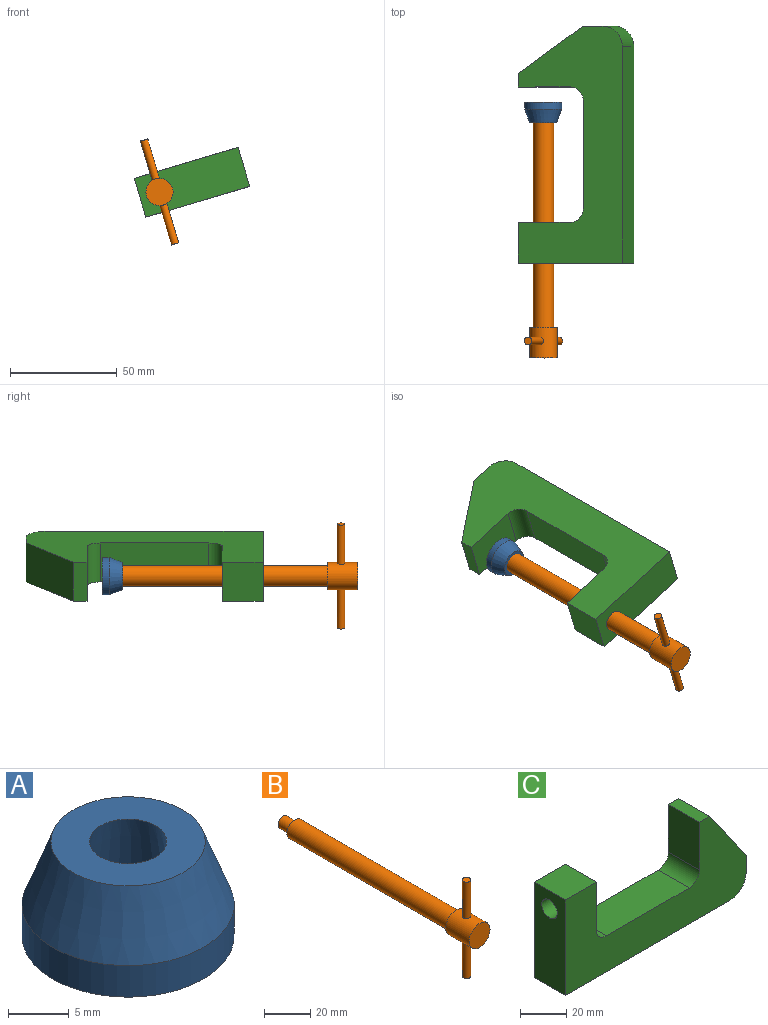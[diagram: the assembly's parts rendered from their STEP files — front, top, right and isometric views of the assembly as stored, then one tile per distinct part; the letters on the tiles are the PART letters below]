
ASSEMBLY  parts=3 mates=3
PART A: 5 faces, bbox 17.4x17.4x9.5 mm
  f0: cylinder r=8.72mm len=17.45mm, axis (0,0,-1), area 174.1mm2, adj f1,f3
  f1: plane 17.45x17.45mm, normal (0,0,-1), area 167.9mm2, adj f0,f4
  f2: plane 12.7x12.7mm, normal (0,0,1), area 95mm2, adj f3,f4
  f3: cone r=8.72mm half-angle=20.5deg, axis (0,0,-1), area 321.1mm2, adj f0,f2
  f4: cone r=4.76mm half-angle=9.5deg, axis (0,0,-1), area 240.8mm2, adj f1,f2
PART B: 11 faces, bbox 12.7x119.8x50.8 mm
  f0: cylinder r=4.76mm len=98.43mm, axis (0,-1,0), area 2945.2mm2, adj f1,f4
  f1: plane 9.53x9.53mm, normal (0,1,0), area 42.1mm2, adj f0,f9
  f2: cylinder r=6.35mm len=14.28mm, axis (0,1,0), area 549.1mm2, adj f3,f4,f6,f7
  f3: plane 12.7x12.7mm, normal (0,-1,0), area 126.7mm2, adj f2
  f4: plane 12.7x12.7mm, normal (0,1,0), area 55.4mm2, adj f0,f2
  f5: plane 3.59x3.59mm, normal (0,0,-1), area 10.1mm2, adj f6
  f6: cylinder r=1.8mm len=19.31mm, axis (0,0,1), area 216.3mm2, adj f2,f5
  f7: cylinder r=1.8mm len=19.31mm, axis (0,0,1), area 216.3mm2, adj f2,f8
  f8: plane 3.59x3.59mm, normal (0,0,1), area 10.1mm2, adj f7
  f9: cylinder r=3.05mm len=7.14mm, axis (0,-1,0), area 136.7mm2, adj f1,f10
  f10: plane 6.1x6.1mm, normal (0,1,0), area 29.2mm2, adj f9
PART C: 15 faces, bbox 111.1x19.1x50.8 mm
  f0: plane 19.05x9.7mm, normal (1,0,0), area 184.9mm2, adj f1,f11,f12,f13
  f1: plane 31.75x22.22mm, normal (0.82,0,0.57), area 738.3mm2, adj f0,f2,f12,f13
  f2: plane 19.05x6.35mm, normal (0,0,1), area 121mm2, adj f1,f3,f12,f13
  f3: plane 25.4x19.05mm, normal (-1,0,0), area 483.9mm2, adj f2,f4,f12,f13
  f4: cylinder r=6.35mm len=19.05mm, axis (0,1,0), area 190mm2, adj f3,f5,f12,f13
  f5: plane 50.8x19.05mm, normal (0,0,1), area 967.7mm2, adj f4,f6,f12,f13
  f6: cylinder r=6.35mm len=19.05mm, axis (0,1,0), area 190mm2, adj f5,f7,f12,f13
  f7: plane 25.4x19.05mm, normal (1,0,0), area 412.6mm2, adj f6,f8,f12,f13,f14
  f8: plane 19.05x19.05mm, normal (0,0,1), area 362.9mm2, adj f7,f9,f12,f13
  f9: plane 50.8x19.05mm, normal (-1,0,0), area 896.5mm2, adj f8,f10,f12,f13,f14
  f10: plane 101.6x19.05mm, normal (0,0,-1), area 1935.5mm2, adj f9,f11,f12,f13
  f11: cylinder r=9.53mm len=19.05mm, axis (0,1,0), area 281.6mm2, adj f0,f10,f12,f13
  f12: plane 111.12x50.8mm, normal (0,-1,0), area 3274mm2, adj f0,f1,f2,f3,f4,f5,f6,f7
  f13: plane 111.12x50.8mm, normal (0,1,0), area 3274mm2, adj f0,f1,f2,f3,f4,f5,f6,f7
  f14: cylinder r=4.76mm len=19.05mm, axis (-1,0,0), area 570mm2, adj f7,f9
PLACE A rot(axis=(0.98,-0.14,0.14),91.2deg) t=(3.07,25.69,62.35)mm
PLACE B rot(axis=(0,-1,0),16.6deg) t=(3.23,-79.87,62.4)mm
PLACE C rot(axis=(-0.63,-0.63,0.47),130deg) t=(55.91,3.51,68.14)mm
MATE pin_slot B.f0 <-> B.f0  axis (0,-1,0) through (3.23,18.55,62.4)mm
MATE pin_slot A.f0 <-> B.f9  axis (0,1,0) through (3.07,25.69,62.35)mm
MATE revolute B.f0 <-> C.f14  axis (0,-1,0) through (3.23,-30.66,62.4)mm
